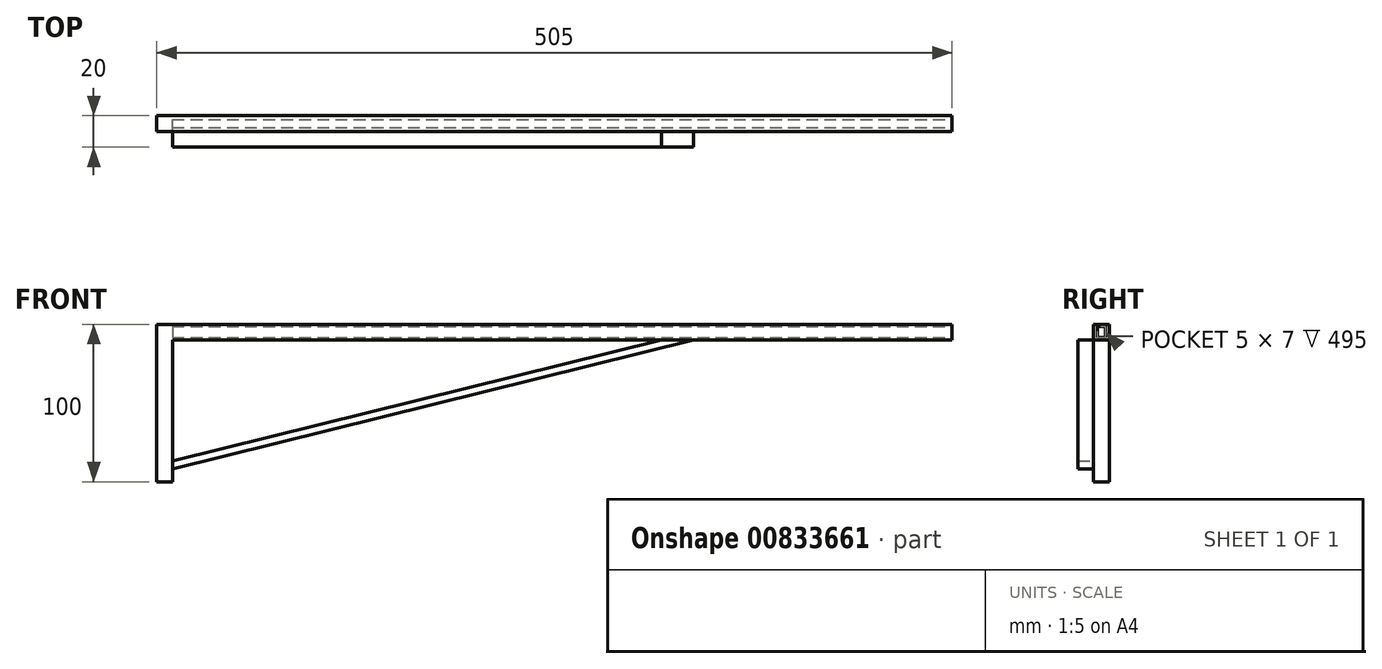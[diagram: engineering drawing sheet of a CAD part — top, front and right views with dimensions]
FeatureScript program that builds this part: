
annotation { "Feature Type Name" : "Feature", "Feature Type Description" : "" }
export const myFeature = defineFeature(function(context is Context, id is Id, definition is map)
    precondition{}
    {
        {
            var Q0;
            Q0=qCreatedBy(makeId("Front.planeOp"),FACE);
            var sketch = newSketch(context, id + "F0", { "sketchPlane" : qUnion([Q0])});
            skLineSegment(sketch, "E0", {"start": v(-79.81, 0) * mm, "end": v(415.19, 0) * mm});
            skLineSegment(sketch, "E1", {"start": v(-79.81, 0) * mm, "end": v(-79.81, -100) * mm});
            skLineSegment(sketch, "E2", {"start": v(-79.81, -100) * mm, "end": v(-89.81, -100) * mm});
            skLineSegment(sketch, "E3", {"start": v(-89.81, -100) * mm, "end": v(-89.81, 0) * mm});
            skLineSegment(sketch, "E4", {"start": v(-89.81, 0) * mm, "end": v(-79.81, 0) * mm});
            skLineSegment(sketch, "E5", {"start": v(415.19, 0) * mm, "end": v(415.19, -10) * mm});
            skLineSegment(sketch, "E6", {"start": v(415.19, -10) * mm, "end": v(-79.81, -10) * mm});
            skSolve(sketch);
        }
        {
            var Q0;
            {var subQ0=sQuery(id+"F0.wireOp",EDGE,"E2");Q0=makeQuery(id+"F0.imprint","IMPRINT",FACE,{"disambiguationData":[TD([[makeQuery(id+"F0.imprint","IMPRINT",EDGE,{"derivedFrom":subQ0}),-1.0]])]});}
            var Q1;
            {var subQ0=sQuery(id+"F0.wireOp",EDGE,"E0");Q1=makeQuery(id+"F0.imprint","IMPRINT",FACE,{"disambiguationData":[TD([[makeQuery(id+"F0.imprint","IMPRINT",EDGE,{"derivedFrom":subQ0}),-1.0]])]});}
            extrude(context, id + "F1", {"entities" : qUnion([Q0, Q1]), "depth" : 10 * mm, "offsetDistance" : 25 * mm});
        }
        {
            var Q0;
            Q0=makeQuery(id+"F1.opExtrude","SWEPT_FACE",FACE,{"disambiguationData":[OSD([sQuery(id+"F0.wireOp",EDGE,"E5")])]});
            var sketch = newSketch(context, id + "F2", { "sketchPlane" : qUnion([Q0])});
            skLineSegment(sketch, "E7", {"start": v(-5, 0) * mm, "end": v(-5, -10) * mm});
            skLineSegment(sketch, "E8", {"start": v(-7.5, -1.5) * mm, "end": v(-7.5, -8.5) * mm});
            skLineSegment(sketch, "E9.MirrorCS", {"start": v(-2.5, -1.5) * mm, "end": v(-2.5, -8.5) * mm});
            skLineSegment(sketch, "E10", {"start": v(-7.5, -1.5) * mm, "end": v(-2.5, -1.5) * mm});
            skLineSegment(sketch, "E11", {"start": v(-7.5, -8.5) * mm, "end": v(-2.5, -8.5) * mm});
            skSolve(sketch);
        }
        {
            var Q0;
            {var subQ5=sQuery(id+"F2.wireOp",EDGE,"E8");Q0=makeQuery(id+"F2.imprint","IMPRINT",FACE,{"disambiguationData":[TD([[makeQuery(id+"F2.imprint","IMPRINT",EDGE,{"derivedFrom":subQ5}),1.0]])]});}
            var Q1;
            {var subQ5=sQuery(id+"F2.wireOp",EDGE,"E9.MirrorCS");Q1=makeQuery(id+"F2.imprint","IMPRINT",FACE,{"disambiguationData":[TD([[makeQuery(id+"F2.imprint","IMPRINT",EDGE,{"derivedFrom":subQ5}),-1.0]])]});}
            extrude(context, id + "F3", {"entities" : qUnion([Q0, Q1]), "operationType" : NewBodyOperationType.REMOVE, "oppositeDirection" : true, "depth" : 495 * mm, "offsetDistance" : 25 * mm});
        }
        {
            var Q0;
            Q0=makeQuery(id+"F1.opExtrude","CAP_FACE",FACE,{"disambiguationData":[OSD([sQuery(id+"F0.wireOp",EDGE,"E0"),sQuery(id+"F0.wireOp",EDGE,"E1"),sQuery(id+"F0.wireOp",EDGE,"E2"),sQuery(id+"F0.wireOp",EDGE,"E3"),sQuery(id+"F0.wireOp",EDGE,"E4"),sQuery(id+"F0.wireOp",EDGE,"E5"),sQuery(id+"F0.wireOp",EDGE,"E6")])],"isStart":false});
            var sketch = newSketch(context, id + "F4", { "sketchPlane" : qUnion([Q0])});
            skLineSegment(sketch, "E12", {"start": v(-79.81, -86.77) * mm, "end": v(230.74, -10) * mm});
            skLineSegment(sketch, "E13", {"start": v(-79.81, -91.77) * mm, "end": v(250.97, -10) * mm});
            skSolve(sketch);
        }
        {
            var Q0;
            {var subQ0=sQuery(id+"F4.wireOp",EDGE,"E12");Q0=makeQuery(id+"F4.imprint","IMPRINT",FACE,{"disambiguationData":[TD([[makeQuery(id+"F4.imprint","IMPRINT",EDGE,{"derivedFrom":subQ0}),-1.0]])]});}
            extrude(context, id + "F5", {"entities" : qUnion([Q0]), "depth" : 10 * mm, "offsetDistance" : 25 * mm});
        }
    });
